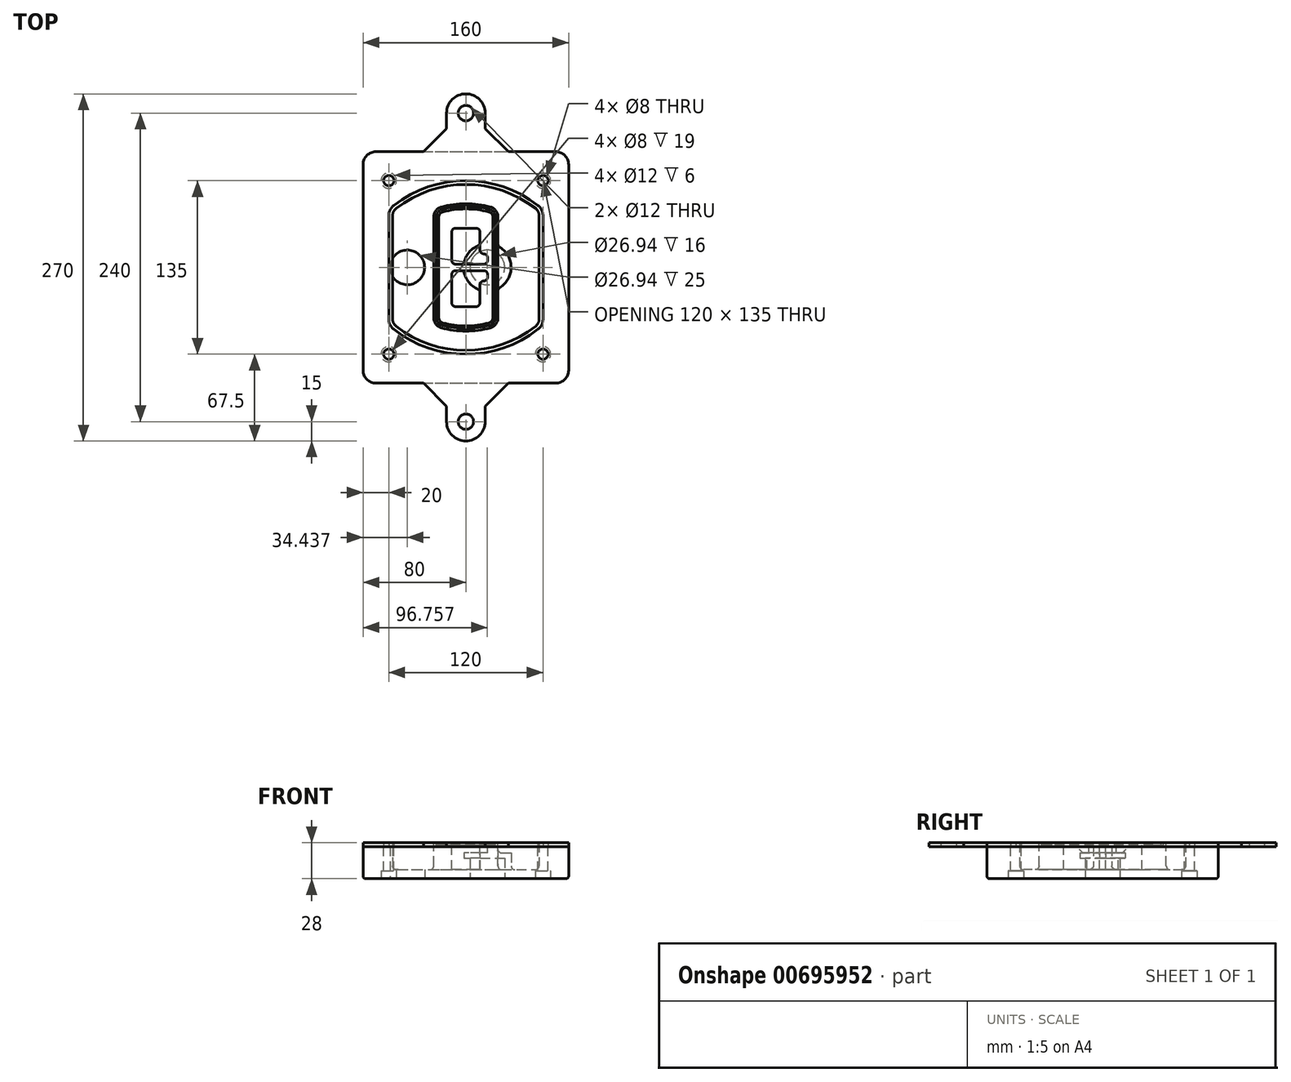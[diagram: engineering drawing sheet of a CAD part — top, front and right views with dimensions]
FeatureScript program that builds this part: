
annotation { "Feature Type Name" : "Feature", "Feature Type Description" : "" }
export const myFeature = defineFeature(function(context is Context, id is Id, definition is map)
    precondition{}
    {
        {
            var Q0;
            Q0=qCreatedBy(makeId("Top.planeOp"),FACE);
            var sketch = newSketch(context, id + "F0", { "sketchPlane" : qUnion([Q0])});
            skPoint(sketch, "E0.rect.middle", {"position": v(0, 0) * mm});
            skLineSegment(sketch, "E1.bottom", {"start": v(-70, -90) * mm, "end": v(70, -90) * mm});
            skLineSegment(sketch, "E1.top", {"start": v(-70, 90) * mm, "end": v(70, 90) * mm});
            skLineSegment(sketch, "E1.left", {"start": v(-80, -80) * mm, "end": v(-80, 80) * mm});
            skLineSegment(sketch, "E1.right", {"start": v(80, -80) * mm, "end": v(80, 80) * mm});
            skLineSegment(sketch, "E2", {"start": v(-80, 90) * mm, "end": v(80, -90) * mm, "construction": true});
            skLineSegment(sketch, "E3", {"start": v(80, 90) * mm, "end": v(-80, -90) * mm, "construction": true});
            skCircle(sketch, "E4", {"center": v(-60, 67.5) * mm, "radius": 4 * mm});
            skCircle(sketch, "E5", {"center": v(60, 67.5) * mm, "radius": 4 * mm});
            skCircle(sketch, "E6", {"center": v(60, -67.5) * mm, "radius": 4 * mm});
            skCircle(sketch, "E7", {"center": v(-60, -67.5) * mm, "radius": 4 * mm});
            skLineSegment(sketch, "E8", {"start": v(-60, 67.5) * mm, "end": v(60, 67.5) * mm, "construction": true});
            skLineSegment(sketch, "E9", {"start": v(60, 67.5) * mm, "end": v(60, -67.5) * mm, "construction": true});
            skLineSegment(sketch, "E10", {"start": v(60, -67.5) * mm, "end": v(-60, -67.5) * mm, "construction": true});
            skLineSegment(sketch, "E11", {"start": v(-60, -67.5) * mm, "end": v(-60, 67.5) * mm, "construction": true});
            skLineSegment(sketch, "E12", {"start": v(-60, 40.3) * mm, "end": v(-60, -40.3) * mm});
            skLineSegment(sketch, "E13", {"start": v(60, 40.3) * mm, "end": v(60, -40.3) * mm});
            skArc(sketch, "E14", {"start": v(56.15, 48.18) * mm, "mid": v(0, 67.5) * mm, "end": v(-56.15, 48.18) * mm});
            skArc(sketch, "E15", {"start": v(-56.15, -48.18) * mm, "mid": v(0, -67.5) * mm, "end": v(56.15, -48.18) * mm});
            skLineSegment(sketch, "E16", {"start": v(-60, 0) * mm, "end": v(60, 0) * mm, "construction": true});
            skPoint(sketch, "E17.visualSharp", {"position": v(-60, -45) * mm});
            skArc(sketch, "E17.filletArc", {"start": v(-60, -40.3) * mm, "mid": v(-58.99, -44.68) * mm, "end": v(-56.15, -48.18) * mm});
            skPoint(sketch, "E18.visualSharp", {"position": v(-60, 45) * mm});
            skArc(sketch, "E18.filletArc", {"start": v(-56.15, 48.18) * mm, "mid": v(-58.99, 44.68) * mm, "end": v(-60, 40.3) * mm});
            skPoint(sketch, "E19.visualSharp", {"position": v(60, 45) * mm});
            skArc(sketch, "E19.filletArc", {"start": v(60, 40.3) * mm, "mid": v(58.99, 44.68) * mm, "end": v(56.15, 48.18) * mm});
            skPoint(sketch, "E20.visualSharp", {"position": v(60, -45) * mm});
            skArc(sketch, "E20.filletArc", {"start": v(56.15, -48.18) * mm, "mid": v(58.99, -44.68) * mm, "end": v(60, -40.3) * mm});
            skPoint(sketch, "E21.visualSharp", {"position": v(-80, 90) * mm});
            skArc(sketch, "E21.filletArc", {"start": v(-70, 90) * mm, "mid": v(-77.07, 87.07) * mm, "end": v(-80, 80) * mm});
            skPoint(sketch, "E22.visualSharp", {"position": v(80, 90) * mm});
            skArc(sketch, "E22.filletArc", {"start": v(80, 80) * mm, "mid": v(77.07, 87.07) * mm, "end": v(70, 90) * mm});
            skPoint(sketch, "E23.visualSharp", {"position": v(80, -90) * mm});
            skArc(sketch, "E23.filletArc", {"start": v(70, -90) * mm, "mid": v(77.07, -87.07) * mm, "end": v(80, -80) * mm});
            skPoint(sketch, "E24.visualSharp", {"position": v(-80, -90) * mm});
            skArc(sketch, "E24.filletArc", {"start": v(-80, -80) * mm, "mid": v(-77.07, -87.07) * mm, "end": v(-70, -90) * mm});
            skArc(sketch, "E25.0", {"start": v(57, 40.3) * mm, "mid": v(56.3, 43.36) * mm, "end": v(54.3, 45.81) * mm});
            skLineSegment(sketch, "E25.1", {"start": v(57, 40.3) * mm, "end": v(57, -40.3) * mm});
            skArc(sketch, "E25.2", {"start": v(54.3, -45.81) * mm, "mid": v(56.3, -43.36) * mm, "end": v(57, -40.3) * mm});
            skArc(sketch, "E25.3", {"start": v(-54.3, -45.81) * mm, "mid": v(0, -64.5) * mm, "end": v(54.3, -45.81) * mm});
            skArc(sketch, "E25.4", {"start": v(-57, -40.3) * mm, "mid": v(-56.3, -43.36) * mm, "end": v(-54.3, -45.81) * mm});
            skArc(sketch, "E25.5", {"start": v(54.3, 45.81) * mm, "mid": v(0, 64.5) * mm, "end": v(-54.3, 45.81) * mm});
            skLineSegment(sketch, "E25.6", {"start": v(-57, 40.3) * mm, "end": v(-57, -40.3) * mm});
            skArc(sketch, "E25.7", {"start": v(-54.3, 45.81) * mm, "mid": v(-56.3, 43.36) * mm, "end": v(-57, 40.3) * mm});
            skArc(sketch, "E26.0", {"start": v(-58.62, 51.33) * mm, "mid": v(-62.58, 46.43) * mm, "end": v(-64, 40.3) * mm});
            skArc(sketch, "E26.1", {"start": v(58.62, 51.33) * mm, "mid": v(0, 71.5) * mm, "end": v(-58.62, 51.33) * mm});
            skArc(sketch, "E26.2", {"start": v(64, 40.3) * mm, "mid": v(62.58, 46.43) * mm, "end": v(58.62, 51.33) * mm});
            skLineSegment(sketch, "E26.3", {"start": v(64, 40.3) * mm, "end": v(64, -40.3) * mm});
            skArc(sketch, "E26.4", {"start": v(58.62, -51.33) * mm, "mid": v(62.58, -46.43) * mm, "end": v(64, -40.3) * mm});
            skLineSegment(sketch, "E26.5", {"start": v(-64, 40.3) * mm, "end": v(-64, -40.3) * mm});
            skArc(sketch, "E26.6", {"start": v(-58.62, -51.33) * mm, "mid": v(0, -71.5) * mm, "end": v(58.62, -51.33) * mm});
            skArc(sketch, "E26.7", {"start": v(-64, -40.3) * mm, "mid": v(-62.58, -46.43) * mm, "end": v(-58.62, -51.33) * mm});
            skSolve(sketch);
        }
        {
            var Q0;
            Q0=makeQuery(id+"F0.imprint","IMPRINT",FACE,{"disambiguationData":[TD([[makeQuery(id+"F0.imprint","IMPRINT",EDGE,{"derivedFrom":sQuery(id+"F0.wireOp",EDGE,"E1.bottom")}),1.0]])]});
            var Q1;
            Q1=makeQuery(id+"F0.imprint","IMPRINT",FACE,{"disambiguationData":[TD([[makeQuery(id+"F0.imprint","IMPRINT",EDGE,{"derivedFrom":sQuery(id+"F0.wireOp",EDGE,"E12")}),1.0]])]});
            var Q2;
            Q2=makeQuery(id+"F0.imprint","IMPRINT",FACE,{"disambiguationData":[TD([[makeQuery(id+"F0.imprint","IMPRINT",EDGE,{"derivedFrom":sQuery(id+"F0.wireOp",EDGE,"E25.0")}),1.0]])]});
            var Q3;
            Q3=makeQuery(id+"F0.imprint","IMPRINT",FACE,{"disambiguationData":[TD([[makeQuery(id+"F0.imprint","IMPRINT",EDGE,{"derivedFrom":sQuery(id+"F0.wireOp",EDGE,"E12")}),-1.0]])]});
            extrude(context, id + "F1", {"entities" : qUnion([Q0, Q1, Q2, Q3]), "oppositeDirection" : true, "depth" : 25 * mm});
        }
        {
            var Q0;
            Q0=makeQuery(id+"F0.imprint","IMPRINT",FACE,{"disambiguationData":[TD([[makeQuery(id+"F0.imprint","IMPRINT",EDGE,{"derivedFrom":sQuery(id+"F0.wireOp",EDGE,"E12")}),1.0]])]});
            extrude(context, id + "F2", {"entities" : qUnion([Q0]), "operationType" : NewBodyOperationType.ADD, "depth" : 3 * mm});
        }
        {
            var Q0;
            Q0=makeQuery(id+"F0.imprint","IMPRINT",FACE,{"disambiguationData":[TD([[makeQuery(id+"F0.imprint","IMPRINT",EDGE,{"derivedFrom":sQuery(id+"F0.wireOp",EDGE,"E25.0")}),1.0]])]});
            extrude(context, id + "F3", {"entities" : qUnion([Q0]), "operationType" : NewBodyOperationType.REMOVE, "oppositeDirection" : true, "depth" : 18 * mm});
        }
        {
            var Q0;
            Q0=makeQuery(id+"F2.opExtrude","CAP_FACE",FACE,{"disambiguationData":[OSD([sQuery(id+"F0.wireOp",EDGE,"E12"),sQuery(id+"F0.wireOp",EDGE,"E13"),sQuery(id+"F0.wireOp",EDGE,"E14"),sQuery(id+"F0.wireOp",EDGE,"E15"),sQuery(id+"F0.wireOp",EDGE,"E17.filletArc"),sQuery(id+"F0.wireOp",EDGE,"E18.filletArc"),sQuery(id+"F0.wireOp",EDGE,"E19.filletArc"),sQuery(id+"F0.wireOp",EDGE,"E20.filletArc"),sQuery(id+"F0.wireOp",EDGE,"E25.0"),sQuery(id+"F0.wireOp",EDGE,"E25.1"),sQuery(id+"F0.wireOp",EDGE,"E25.2"),sQuery(id+"F0.wireOp",EDGE,"E25.3"),sQuery(id+"F0.wireOp",EDGE,"E25.4"),sQuery(id+"F0.wireOp",EDGE,"E25.5"),sQuery(id+"F0.wireOp",EDGE,"E25.6"),sQuery(id+"F0.wireOp",EDGE,"E25.7")])],"isStart":false});
            var sketch = newSketch(context, id + "F4", { "sketchPlane" : qUnion([Q0])});
            skArc(sketch, "E27.0", {"start": v(-19.08, -46.97) * mm, "mid": v(0, -49.5) * mm, "end": v(19.08, -46.97) * mm});
            skArc(sketch, "E28.0", {"start": v(19.08, 46.97) * mm, "mid": v(0, 49.5) * mm, "end": v(-19.08, 46.97) * mm});
            skLineSegment(sketch, "E29", {"start": v(-25, 39.25) * mm, "end": v(-25, -39.25) * mm});
            skLineSegment(sketch, "E30", {"start": v(25, 39.25) * mm, "end": v(25, -39.25) * mm});
            skLineSegment(sketch, "E31", {"start": v(-25, 45.1) * mm, "end": v(25, 45.1) * mm, "construction": true});
            skLineSegment(sketch, "E32", {"start": v(-25, -45.1) * mm, "end": v(25, -45.1) * mm, "construction": true});
            skPoint(sketch, "E33.visualSharp", {"position": v(-25, 45.1) * mm});
            skArc(sketch, "E33.filletArc", {"start": v(-19.08, 46.97) * mm, "mid": v(-23.35, 44.11) * mm, "end": v(-25, 39.25) * mm});
            skPoint(sketch, "E34.visualSharp", {"position": v(25, 45.1) * mm});
            skArc(sketch, "E34.filletArc", {"start": v(25, 39.25) * mm, "mid": v(23.35, 44.11) * mm, "end": v(19.08, 46.97) * mm});
            skPoint(sketch, "E35.visualSharp", {"position": v(25, -45.1) * mm});
            skArc(sketch, "E35.filletArc", {"start": v(19.08, -46.97) * mm, "mid": v(23.35, -44.11) * mm, "end": v(25, -39.25) * mm});
            skPoint(sketch, "E36.visualSharp", {"position": v(-25, -45.1) * mm});
            skArc(sketch, "E36.filletArc", {"start": v(-25, -39.25) * mm, "mid": v(-23.35, -44.11) * mm, "end": v(-19.08, -46.97) * mm});
            skArc(sketch, "E37.0", {"start": v(54.3, 45.81) * mm, "mid": v(0, 64.5) * mm, "end": v(-54.3, 45.81) * mm});
            skArc(sketch, "E37.1", {"start": v(-54.3, 45.81) * mm, "mid": v(-56.3, 43.36) * mm, "end": v(-57, 40.3) * mm});
            skLineSegment(sketch, "E37.2", {"start": v(-57, 40.3) * mm, "end": v(-57, -40.3) * mm});
            skArc(sketch, "E37.3", {"start": v(-57, -40.3) * mm, "mid": v(-56.3, -43.36) * mm, "end": v(-54.3, -45.81) * mm});
            skArc(sketch, "E37.4", {"start": v(-54.3, -45.81) * mm, "mid": v(0, -64.5) * mm, "end": v(54.3, -45.81) * mm});
            skArc(sketch, "E37.5", {"start": v(54.3, -45.81) * mm, "mid": v(56.3, -43.36) * mm, "end": v(57, -40.3) * mm});
            skLineSegment(sketch, "E37.6", {"start": v(57, 40.3) * mm, "end": v(57, -40.3) * mm});
            skArc(sketch, "E37.7", {"start": v(57, 40.3) * mm, "mid": v(56.3, 43.36) * mm, "end": v(54.3, 45.81) * mm});
            skLineSegment(sketch, "E38.0", {"start": v(23, 39.25) * mm, "end": v(23, -39.25) * mm});
            skArc(sketch, "E38.1", {"start": v(18.56, -45.04) * mm, "mid": v(21.76, -42.9) * mm, "end": v(23, -39.25) * mm});
            skArc(sketch, "E38.2", {"start": v(-18.56, -45.04) * mm, "mid": v(0, -47.5) * mm, "end": v(18.56, -45.04) * mm});
            skArc(sketch, "E38.3", {"start": v(-23, -39.25) * mm, "mid": v(-21.76, -42.9) * mm, "end": v(-18.56, -45.04) * mm});
            skLineSegment(sketch, "E38.4", {"start": v(-23, 39.25) * mm, "end": v(-23, -39.25) * mm});
            skArc(sketch, "E38.5", {"start": v(23, 39.25) * mm, "mid": v(21.76, 42.9) * mm, "end": v(18.56, 45.04) * mm});
            skArc(sketch, "E38.6", {"start": v(-18.56, 45.04) * mm, "mid": v(-21.76, 42.9) * mm, "end": v(-23, 39.25) * mm});
            skArc(sketch, "E38.7", {"start": v(18.56, 45.04) * mm, "mid": v(0, 47.5) * mm, "end": v(-18.56, 45.04) * mm});
            skArc(sketch, "E39.0", {"start": v(21, 39.25) * mm, "mid": v(20.18, 41.68) * mm, "end": v(18.04, 43.1) * mm});
            skLineSegment(sketch, "E39.1", {"start": v(21, 39.25) * mm, "end": v(21, -39.25) * mm});
            skArc(sketch, "E39.2", {"start": v(18.04, -43.1) * mm, "mid": v(20.18, -41.68) * mm, "end": v(21, -39.25) * mm});
            skArc(sketch, "E39.3", {"start": v(-18.04, -43.1) * mm, "mid": v(0, -45.5) * mm, "end": v(18.04, -43.1) * mm});
            skArc(sketch, "E39.4", {"start": v(-21, -39.25) * mm, "mid": v(-20.18, -41.68) * mm, "end": v(-18.04, -43.1) * mm});
            skArc(sketch, "E39.5", {"start": v(18.04, 43.1) * mm, "mid": v(0, 45.5) * mm, "end": v(-18.04, 43.1) * mm});
            skLineSegment(sketch, "E39.6", {"start": v(-21, 39.25) * mm, "end": v(-21, -39.25) * mm});
            skArc(sketch, "E39.7", {"start": v(-18.04, 43.1) * mm, "mid": v(-20.18, 41.68) * mm, "end": v(-21, 39.25) * mm});
            skLineSegment(sketch, "E40", {"start": v(-25, 0) * mm, "end": v(25, 0) * mm, "construction": true});
            skLineSegment(sketch, "E41", {"start": v(-11, 5.5) * mm, "end": v(-11, 27.5) * mm});
            skLineSegment(sketch, "E42", {"start": v(-8, 30.5) * mm, "end": v(8, 30.5) * mm});
            skLineSegment(sketch, "E43", {"start": v(11, 27.5) * mm, "end": v(11, 13.5) * mm});
            skLineSegment(sketch, "E44", {"start": v(14, 10.5) * mm, "end": v(14, 10.5) * mm});
            skLineSegment(sketch, "E45", {"start": v(17, 7.5) * mm, "end": v(17, 5.5) * mm});
            skLineSegment(sketch, "E46", {"start": v(14, 2.5) * mm, "end": v(-8, 2.5) * mm});
            skPoint(sketch, "E47.visualSharp", {"position": v(-11, 30.5) * mm});
            skArc(sketch, "E47.filletArc", {"start": v(-8, 30.5) * mm, "mid": v(-10.12, 29.62) * mm, "end": v(-11, 27.5) * mm});
            skPoint(sketch, "E48.visualSharp", {"position": v(11, 30.5) * mm});
            skArc(sketch, "E48.filletArc", {"start": v(11, 27.5) * mm, "mid": v(10.12, 29.62) * mm, "end": v(8, 30.5) * mm});
            skPoint(sketch, "E49.visualSharp", {"position": v(11, 10.5) * mm});
            skArc(sketch, "E49.filletArc", {"start": v(11, 13.5) * mm, "mid": v(11.88, 11.38) * mm, "end": v(14, 10.5) * mm});
            skPoint(sketch, "E50.visualSharp", {"position": v(17, 10.5) * mm});
            skArc(sketch, "E50.filletArc", {"start": v(17, 7.5) * mm, "mid": v(16.12, 9.62) * mm, "end": v(14, 10.5) * mm});
            skPoint(sketch, "E51.visualSharp", {"position": v(17, 2.5) * mm});
            skArc(sketch, "E51.filletArc", {"start": v(14, 2.5) * mm, "mid": v(16.12, 3.38) * mm, "end": v(17, 5.5) * mm});
            skPoint(sketch, "E52.visualSharp", {"position": v(-11, 2.5) * mm});
            skArc(sketch, "E52.filletArc", {"start": v(-11, 5.5) * mm, "mid": v(-10.12, 3.38) * mm, "end": v(-8, 2.5) * mm});
            skLineSegment(sketch, "E53.0.MirrorCS", {"start": v(14, -2.5) * mm, "end": v(-8, -2.5) * mm});
            skArc(sketch, "E54.0.MirrorCS", {"start": v(-11, -5.5) * mm, "mid": v(-10.12, -3.38) * mm, "end": v(-8, -2.5) * mm});
            skLineSegment(sketch, "E55.0.MirrorCS", {"start": v(-11, -5.5) * mm, "end": v(-11, -27.5) * mm});
            skArc(sketch, "E56.0.MirrorCS", {"start": v(-8, -30.5) * mm, "mid": v(-10.12, -29.62) * mm, "end": v(-11, -27.5) * mm});
            skLineSegment(sketch, "E57.0.MirrorCS", {"start": v(-8, -30.5) * mm, "end": v(8, -30.5) * mm});
            skArc(sketch, "E58.0.MirrorCS", {"start": v(11, -27.5) * mm, "mid": v(10.12, -29.62) * mm, "end": v(8, -30.5) * mm});
            skLineSegment(sketch, "E59.0.MirrorCS", {"start": v(11, -27.5) * mm, "end": v(11, -13.5) * mm});
            skArc(sketch, "E60.0.MirrorCS", {"start": v(11, -13.5) * mm, "mid": v(11.88, -11.38) * mm, "end": v(14, -10.5) * mm});
            skArc(sketch, "E61.0.MirrorCS", {"start": v(17, -7.5) * mm, "mid": v(16.12, -9.62) * mm, "end": v(14, -10.5) * mm});
            skLineSegment(sketch, "E62.0.MirrorCS", {"start": v(17, -7.5) * mm, "end": v(17, -5.5) * mm});
            skArc(sketch, "E63.0.MirrorCS", {"start": v(14, -2.5) * mm, "mid": v(16.12, -3.38) * mm, "end": v(17, -5.5) * mm});
            skSolve(sketch);
        }
        {
            var Q0;
            Q0=makeQuery(id+"F4.imprint","IMPRINT",FACE,{"disambiguationData":[TD([[makeQuery(id+"F4.imprint","IMPRINT",EDGE,{"derivedFrom":sQuery(id+"F4.wireOp",EDGE,"E27.0")}),1.0]])]});
            var Q1;
            Q1=makeQuery(id+"F4.imprint","IMPRINT",FACE,{"disambiguationData":[TD([[makeQuery(id+"F4.imprint","IMPRINT",EDGE,{"derivedFrom":sQuery(id+"F4.wireOp",EDGE,"E38.0")}),-1.0]])]});
            var Q2;
            Q2=makeQuery(id+"F4.imprint","IMPRINT",FACE,{"disambiguationData":[TD([[makeQuery(id+"F4.imprint","IMPRINT",EDGE,{"derivedFrom":sQuery(id+"F4.wireOp",EDGE,"E39.0")}),1.0]])]});
            extrude(context, id + "F5", {"entities" : qUnion([Q0, Q1, Q2]), "operationType" : NewBodyOperationType.ADD, "endBound" : BoundingType.UP_TO_NEXT, "oppositeDirection" : true, "depth" : 25 * mm});
        }
        {
            var Q0;
            Q0=makeQuery(id+"F4.imprint","IMPRINT",FACE,{"disambiguationData":[TD([[makeQuery(id+"F4.imprint","IMPRINT",EDGE,{"derivedFrom":sQuery(id+"F4.wireOp",EDGE,"E38.0")}),-1.0]])]});
            extrude(context, id + "F6", {"entities" : qUnion([Q0]), "operationType" : NewBodyOperationType.REMOVE, "oppositeDirection" : true, "depth" : 2 * mm});
        }
        {
            var Q0;
            Q0=makeQuery(id+"F1.opExtrude","CAP_FACE",FACE,{"disambiguationData":[OSD([sQuery(id+"F0.wireOp",EDGE,"E1.bottom"),sQuery(id+"F0.wireOp",EDGE,"E1.top"),sQuery(id+"F0.wireOp",EDGE,"E1.left"),sQuery(id+"F0.wireOp",EDGE,"E1.right"),sQuery(id+"F0.wireOp",EDGE,"E4"),sQuery(id+"F0.wireOp",EDGE,"E5"),sQuery(id+"F0.wireOp",EDGE,"E6"),sQuery(id+"F0.wireOp",EDGE,"E7"),sQuery(id+"F0.wireOp",EDGE,"E21.filletArc"),sQuery(id+"F0.wireOp",EDGE,"E22.filletArc"),sQuery(id+"F0.wireOp",EDGE,"E23.filletArc"),sQuery(id+"F0.wireOp",EDGE,"E24.filletArc")])],"isStart":false});
            var sketch = newSketch(context, id + "F7", { "sketchPlane" : qUnion([Q0])});
            skCircle(sketch, "E64", {"center": v(16.76, 0) * mm, "radius": 13.47 * mm});
            skCircle(sketch, "E65", {"center": v(-45.56, 0) * mm, "radius": 13.47 * mm});
            skLineSegment(sketch, "E66", {"start": v(80, 0) * mm, "end": v(-80, 0) * mm});
            skCircle(sketch, "E67", {"center": v(16.76, 0) * mm, "radius": 18.47 * mm});
            skCircle(sketch, "E68", {"center": v(60, -67.5) * mm, "radius": 6 * mm});
            skCircle(sketch, "E69", {"center": v(-60, -67.5) * mm, "radius": 6 * mm});
            skCircle(sketch, "E70", {"center": v(-60, 67.5) * mm, "radius": 6 * mm});
            skCircle(sketch, "E71", {"center": v(60, 67.5) * mm, "radius": 6 * mm});
            skSolve(sketch);
        }
        {
            var Q0;
            {var subQ1=sQuery(id+"F7.wireOp",EDGE,"E66");var subQ4=sQuery(id+"F7.wireOp",EDGE,"E64");var subQ6=makeQuery(id+"F7.imprint","INTERSECT",VERTEX,{"disambiguationData":[OD(0.0)],"derivedFrom":[subQ4,subQ1]});Q0=makeQuery(id+"F7.imprint","IMPRINT",FACE,{"disambiguationData":[TD([[makeQuery(id+"F7.imprint","IMPRINT",EDGE,{"disambiguationData":[TD([[subQ6,-1.0]])],"derivedFrom":subQ4}),-1.0]])]});}
            var Q1;
            {var subQ0=sQuery(id+"F7.wireOp",EDGE,"E66");var subQ1=sQuery(id+"F7.wireOp",EDGE,"E64");var subQ3=makeQuery(id+"F7.imprint","INTERSECT",VERTEX,{"disambiguationData":[OD(0.0)],"derivedFrom":[subQ1,subQ0]});Q1=makeQuery(id+"F7.imprint","IMPRINT",FACE,{"disambiguationData":[TD([[makeQuery(id+"F7.imprint","IMPRINT",EDGE,{"disambiguationData":[TD([[subQ3,-1.0]])],"derivedFrom":subQ1}),1.0]])]});}
            var Q2;
            {var subQ0=sQuery(id+"F7.wireOp",EDGE,"E66");var subQ1=sQuery(id+"F7.wireOp",EDGE,"E64");var subQ3=makeQuery(id+"F7.imprint","INTERSECT",VERTEX,{"disambiguationData":[OD(0.0)],"derivedFrom":[subQ1,subQ0]});Q2=makeQuery(id+"F7.imprint","IMPRINT",FACE,{"disambiguationData":[TD([[makeQuery(id+"F7.imprint","IMPRINT",EDGE,{"disambiguationData":[TD([[subQ3,1.0]])],"derivedFrom":subQ1}),1.0]])]});}
            var Q3;
            {var subQ1=sQuery(id+"F7.wireOp",EDGE,"E66");var subQ4=sQuery(id+"F7.wireOp",EDGE,"E64");var subQ6=makeQuery(id+"F7.imprint","INTERSECT",VERTEX,{"disambiguationData":[OD(0.0)],"derivedFrom":[subQ4,subQ1]});Q3=makeQuery(id+"F7.imprint","IMPRINT",FACE,{"disambiguationData":[TD([[makeQuery(id+"F7.imprint","IMPRINT",EDGE,{"disambiguationData":[TD([[subQ6,1.0]])],"derivedFrom":subQ4}),-1.0]])]});}
            extrude(context, id + "F8", {"entities" : qUnion([Q0, Q1, Q2, Q3]), "operationType" : NewBodyOperationType.ADD, "oppositeDirection" : true, "depth" : 20 * mm});
        }
        {
            var Q0;
            {var subQ0=sQuery(id+"F7.wireOp",EDGE,"E66");var subQ1=sQuery(id+"F7.wireOp",EDGE,"E64");var subQ3=makeQuery(id+"F7.imprint","INTERSECT",VERTEX,{"disambiguationData":[OD(0.0)],"derivedFrom":[subQ1,subQ0]});Q0=makeQuery(id+"F7.imprint","IMPRINT",FACE,{"disambiguationData":[TD([[makeQuery(id+"F7.imprint","IMPRINT",EDGE,{"disambiguationData":[TD([[subQ3,-1.0]])],"derivedFrom":subQ1}),1.0]])]});}
            var Q1;
            {var subQ0=sQuery(id+"F7.wireOp",EDGE,"E66");var subQ1=sQuery(id+"F7.wireOp",EDGE,"E64");var subQ3=makeQuery(id+"F7.imprint","INTERSECT",VERTEX,{"disambiguationData":[OD(0.0)],"derivedFrom":[subQ1,subQ0]});Q1=makeQuery(id+"F7.imprint","IMPRINT",FACE,{"disambiguationData":[TD([[makeQuery(id+"F7.imprint","IMPRINT",EDGE,{"disambiguationData":[TD([[subQ3,1.0]])],"derivedFrom":subQ1}),1.0]])]});}
            extrude(context, id + "F9", {"entities" : qUnion([Q0, Q1]), "operationType" : NewBodyOperationType.REMOVE, "oppositeDirection" : true, "depth" : 16 * mm});
        }
        {
            var Q0;
            {var subQ0=sQuery(id+"F7.wireOp",EDGE,"E66");var subQ1=sQuery(id+"F7.wireOp",EDGE,"E65");var subQ3=makeQuery(id+"F7.imprint","INTERSECT",VERTEX,{"disambiguationData":[OD(0.0)],"derivedFrom":[subQ1,subQ0]});Q0=makeQuery(id+"F7.imprint","IMPRINT",FACE,{"disambiguationData":[TD([[makeQuery(id+"F7.imprint","IMPRINT",EDGE,{"disambiguationData":[TD([[subQ3,-1.0]])],"derivedFrom":subQ1}),1.0]])]});}
            var Q1;
            {var subQ0=sQuery(id+"F7.wireOp",EDGE,"E66");var subQ1=sQuery(id+"F7.wireOp",EDGE,"E65");var subQ3=makeQuery(id+"F7.imprint","INTERSECT",VERTEX,{"disambiguationData":[OD(0.0)],"derivedFrom":[subQ1,subQ0]});Q1=makeQuery(id+"F7.imprint","IMPRINT",FACE,{"disambiguationData":[TD([[makeQuery(id+"F7.imprint","IMPRINT",EDGE,{"disambiguationData":[TD([[subQ3,1.0]])],"derivedFrom":subQ1}),1.0]])]});}
            extrude(context, id + "F10", {"entities" : qUnion([Q0, Q1]), "operationType" : NewBodyOperationType.REMOVE, "oppositeDirection" : true, "depth" : 25 * mm});
        }
        {
            var Q0;
            Q0=makeQuery(id+"F7.imprint","IMPRINT",FACE,{"disambiguationData":[TD([[makeQuery(id+"F7.imprint","IMPRINT",EDGE,{"derivedFrom":sQuery(id+"F7.wireOp",EDGE,"E68")}),1.0]])]});
            var Q1;
            Q1=makeQuery(id+"F7.imprint","IMPRINT",FACE,{"disambiguationData":[TD([[makeQuery(id+"F7.imprint","IMPRINT",EDGE,{"derivedFrom":makeQuery(id+"F1.opExtrude","CAP_EDGE",EDGE,{"disambiguationData":[OSD([sQuery(id+"F0.wireOp",EDGE,"E5")])],"isStart":false})}),-1.0]])]});
            var Q2;
            Q2=makeQuery(id+"F7.imprint","IMPRINT",FACE,{"disambiguationData":[TD([[makeQuery(id+"F7.imprint","IMPRINT",EDGE,{"derivedFrom":sQuery(id+"F7.wireOp",EDGE,"E69")}),1.0]])]});
            var Q3;
            Q3=makeQuery(id+"F7.imprint","IMPRINT",FACE,{"disambiguationData":[TD([[makeQuery(id+"F7.imprint","IMPRINT",EDGE,{"derivedFrom":makeQuery(id+"F1.opExtrude","CAP_EDGE",EDGE,{"disambiguationData":[OSD([sQuery(id+"F0.wireOp",EDGE,"E4")])],"isStart":false})}),-1.0]])]});
            var Q4;
            Q4=makeQuery(id+"F7.imprint","IMPRINT",FACE,{"disambiguationData":[TD([[makeQuery(id+"F7.imprint","IMPRINT",EDGE,{"derivedFrom":sQuery(id+"F7.wireOp",EDGE,"E70")}),1.0]])]});
            var Q5;
            Q5=makeQuery(id+"F7.imprint","IMPRINT",FACE,{"disambiguationData":[TD([[makeQuery(id+"F7.imprint","IMPRINT",EDGE,{"derivedFrom":makeQuery(id+"F1.opExtrude","CAP_EDGE",EDGE,{"disambiguationData":[OSD([sQuery(id+"F0.wireOp",EDGE,"E7")])],"isStart":false})}),-1.0]])]});
            var Q6;
            Q6=makeQuery(id+"F7.imprint","IMPRINT",FACE,{"disambiguationData":[TD([[makeQuery(id+"F7.imprint","IMPRINT",EDGE,{"derivedFrom":sQuery(id+"F7.wireOp",EDGE,"E71")}),1.0]])]});
            var Q7;
            Q7=makeQuery(id+"F7.imprint","IMPRINT",FACE,{"disambiguationData":[TD([[makeQuery(id+"F7.imprint","IMPRINT",EDGE,{"derivedFrom":makeQuery(id+"F1.opExtrude","CAP_EDGE",EDGE,{"disambiguationData":[OSD([sQuery(id+"F0.wireOp",EDGE,"E6")])],"isStart":false})}),-1.0]])]});
            extrude(context, id + "F11", {"entities" : qUnion([Q0, Q1, Q2, Q3, Q4, Q5, Q6, Q7]), "operationType" : NewBodyOperationType.REMOVE, "oppositeDirection" : true, "depth" : 6 * mm});
        }
        {
            var Q0;
            Q0=makeQuery(id+"F9.boolean.opBoolean","COPY",FACE,{"derivedFrom":makeQuery(id+"F9.opExtrude","CAP_FACE",FACE,{"disambiguationData":[OSD([sQuery(id+"F7.wireOp",EDGE,"E64")])],"isStart":false})});
            var sketch = newSketch(context, id + "F12", { "sketchPlane" : qUnion([Q0])});
            skArc(sketch, "E72.0", {"start": v(11, 17.55) * mm, "mid": v(2.57, 11.82) * mm, "end": v(-1.54, 2.5) * mm});
            skArc(sketch, "E72.1", {"start": v(-1.54, -2.5) * mm, "mid": v(2.57, -11.82) * mm, "end": v(11, -17.55) * mm});
            skLineSegment(sketch, "E73", {"start": v(-1.54, -2.5) * mm, "end": v(14, -2.5) * mm});
            skLineSegment(sketch, "E74.0", {"start": v(14, 2.5) * mm, "end": v(-1.54, 2.5) * mm});
            skArc(sketch, "E74.1", {"start": v(14, 2.5) * mm, "mid": v(16.12, 3.38) * mm, "end": v(17, 5.5) * mm});
            skLineSegment(sketch, "E74.2", {"start": v(17, 7.5) * mm, "end": v(17, 5.5) * mm});
            skArc(sketch, "E74.3", {"start": v(17, 7.5) * mm, "mid": v(16.12, 9.62) * mm, "end": v(14, 10.5) * mm});
            skArc(sketch, "E74.4", {"start": v(11, 13.5) * mm, "mid": v(11.88, 11.38) * mm, "end": v(14, 10.5) * mm});
            skLineSegment(sketch, "E74.5", {"start": v(11, 17.55) * mm, "end": v(11, 13.5) * mm});
            skLineSegment(sketch, "E74.7", {"start": v(14, -2.5) * mm, "end": v(-1.54, -2.5) * mm});
            skArc(sketch, "E74.8", {"start": v(14, -2.5) * mm, "mid": v(16.12, -3.38) * mm, "end": v(17, -5.5) * mm});
            skLineSegment(sketch, "E74.9", {"start": v(17, -7.5) * mm, "end": v(17, -5.5) * mm});
            skArc(sketch, "E74.10", {"start": v(17, -7.5) * mm, "mid": v(16.12, -9.62) * mm, "end": v(14, -10.5) * mm});
            skArc(sketch, "E74.11", {"start": v(11, -13.5) * mm, "mid": v(11.88, -11.38) * mm, "end": v(14, -10.5) * mm});
            skLineSegment(sketch, "E74.12", {"start": v(11, -17.55) * mm, "end": v(11, -13.5) * mm});
            skPoint(sketch, "E75.orphan", {"position": v(11, -27.5) * mm});
            skPoint(sketch, "E76.orphan", {"position": v(-8, -2.5) * mm});
            skPoint(sketch, "E77.orphan", {"position": v(-8, 2.5) * mm});
            skPoint(sketch, "E78.orphan", {"position": v(11, 27.5) * mm});
            skSolve(sketch);
        }
        {
            var Q0;
            {var subQ7=sQuery(id+"F12.wireOp",EDGE,"E72.0");var subQ14=sQuery(id+"F12.wireOp",EDGE,"E72.1");var subQ16=sQuery(id+"F12.wireOp",EDGE,"E74.1");var subQ18=sQuery(id+"F12.wireOp",EDGE,"E74.8");Q0=qUnion([makeQuery(id+"F12.imprint","IMPRINT",FACE,{"disambiguationData":[TD([[makeQuery(id+"F12.imprint","IMPRINT",EDGE,{"derivedFrom":subQ7}),1.0]])]}),makeQuery(id+"F12.imprint","IMPRINT",FACE,{"disambiguationData":[TD([[makeQuery(id+"F12.imprint","IMPRINT",EDGE,{"derivedFrom":subQ14}),1.0]])]}),makeQuery(id+"F12.imprint","IMPRINT",FACE,{"disambiguationData":[TD([[makeQuery(id+"F12.imprint","IMPRINT",EDGE,{"derivedFrom":subQ16}),1.0]])]}),makeQuery(id+"F12.imprint","IMPRINT",FACE,{"disambiguationData":[TD([[makeQuery(id+"F12.imprint","IMPRINT",EDGE,{"derivedFrom":subQ18}),-1.0]])]})]);}
            var Q1;
            Q1=makeQuery(id+"F5.boolean.opBoolean","SPLIT",FACE,{"disambiguationData":[TD([makeQuery(id+"F5.opExtrude","SWEPT_FACE",FACE,{"disambiguationData":[OSD([sQuery(id+"F4.wireOp",EDGE,"E41")])]})])],"derivedFrom":makeQuery(id+"F3.boolean.opBoolean","COPY",FACE,{"derivedFrom":makeQuery(id+"F3.opExtrude","CAP_FACE",FACE,{"disambiguationData":[OSD([sQuery(id+"F0.wireOp",EDGE,"E25.0"),sQuery(id+"F0.wireOp",EDGE,"E25.1"),sQuery(id+"F0.wireOp",EDGE,"E25.2"),sQuery(id+"F0.wireOp",EDGE,"E25.3"),sQuery(id+"F0.wireOp",EDGE,"E25.4"),sQuery(id+"F0.wireOp",EDGE,"E25.5"),sQuery(id+"F0.wireOp",EDGE,"E25.6"),sQuery(id+"F0.wireOp",EDGE,"E25.7")])],"isStart":false})})});
            extrude(context, id + "F13", {"entities" : qUnion([Q0]), "operationType" : NewBodyOperationType.REMOVE, "endBound" : BoundingType.UP_TO_SURFACE, "endBoundEntityFace" : qUnion([Q1]), "depth" : 25 * mm});
        }
        {
            var Q0;
            Q0=makeQuery(id+"F3.boolean.opBoolean","COPY",EDGE,{"derivedFrom":makeQuery(id+"F3.opExtrude","CAP_EDGE",EDGE,{"disambiguationData":[OSD([sQuery(id+"F0.wireOp",EDGE,"E25.6")])],"isStart":false})});
            var Q1;
            Q1=makeQuery(id+"F8.boolean.opBoolean","INTERSECT",EDGE,{"derivedFrom":[makeQuery(id+"F5.opExtrude","SWEPT_FACE",FACE,{"disambiguationData":[OSD([sQuery(id+"F4.wireOp",EDGE,"E30")])]}),makeQuery(id+"F8.opExtrude","CAP_FACE",FACE,{"disambiguationData":[OSD([sQuery(id+"F7.wireOp",EDGE,"E67")])],"isStart":false})]});
            var Q2;
            Q2=makeQuery(id+"F8.boolean.opBoolean","INTERSECT",EDGE,{"disambiguationData":[OD(1.0)],"derivedFrom":[makeQuery(id+"F5.opExtrude","SWEPT_FACE",FACE,{"disambiguationData":[OSD([sQuery(id+"F4.wireOp",EDGE,"E30")])]}),makeQuery(id+"F8.opExtrude","SWEPT_FACE",FACE,{"disambiguationData":[OSD([sQuery(id+"F7.wireOp",EDGE,"E67")])]})]});
            var Q3;
            {var subQ0=sQuery(id+"F4.wireOp",EDGE,"E30");Q3=makeQuery(id+"F8.boolean.opBoolean","SPLIT",EDGE,{"disambiguationData":[TD([makeQuery(id+"F5.opExtrude","SWEPT_FACE",FACE,{"disambiguationData":[OSD([sQuery(id+"F4.wireOp",EDGE,"E35.filletArc")])]})])],"derivedFrom":makeQuery(id+"F5.opExtrude","CAP_EDGE",EDGE,{"disambiguationData":[OSD([subQ0])],"isStart":false})});}
            var Q4;
            {var subQ0=sQuery(id+"F0.wireOp",EDGE,"E25.7");var subQ1=sQuery(id+"F0.wireOp",EDGE,"E25.1");var subQ2=sQuery(id+"F0.wireOp",EDGE,"E25.6");var subQ3=sQuery(id+"F0.wireOp",EDGE,"E25.5");var subQ4=sQuery(id+"F0.wireOp",EDGE,"E25.4");var subQ5=sQuery(id+"F0.wireOp",EDGE,"E25.0");var subQ6=sQuery(id+"F0.wireOp",EDGE,"E25.2");var subQ7=sQuery(id+"F0.wireOp",EDGE,"E25.3");Q4=makeQuery(id+"F8.boolean.opBoolean","INTERSECT",EDGE,{"derivedFrom":[makeQuery(id+"F5.boolean.opBoolean","SPLIT",FACE,{"disambiguationData":[TD([makeQuery(id+"F2.opExtrude","SWEPT_FACE",FACE,{"disambiguationData":[OSD([subQ5])]})])],"derivedFrom":makeQuery(id+"F3.boolean.opBoolean","COPY",FACE,{"derivedFrom":makeQuery(id+"F3.opExtrude","CAP_FACE",FACE,{"disambiguationData":[OSD([subQ5,subQ1,subQ6,subQ7,subQ4,subQ3,subQ2,subQ0])],"isStart":false})})}),makeQuery(id+"F8.opExtrude","SWEPT_FACE",FACE,{"disambiguationData":[OSD([sQuery(id+"F7.wireOp",EDGE,"E67")])]})]});}
            var Q5;
            Q5=makeQuery(id+"F8.boolean.opBoolean","INTERSECT",EDGE,{"disambiguationData":[OD(0.0)],"derivedFrom":[makeQuery(id+"F5.opExtrude","SWEPT_FACE",FACE,{"disambiguationData":[OSD([sQuery(id+"F4.wireOp",EDGE,"E30")])]}),makeQuery(id+"F8.opExtrude","SWEPT_FACE",FACE,{"disambiguationData":[OSD([sQuery(id+"F7.wireOp",EDGE,"E67")])]})]});
            fillet(context, id + "F14", {"entities" : qUnion([Q0, Q1, Q2, Q3, Q4, Q5]), "radius" : 3 * mm, "tangentPropagation" : true, "allowEdgeOverflow" : false});
        }
        {
            var Q0;
            Q0=makeQuery(id+"F1.opExtrude","CAP_EDGE",EDGE,{"disambiguationData":[OSD([sQuery(id+"F0.wireOp",EDGE,"E1.bottom")])],"isStart":false});
            fillet(context, id + "F15", {"entities" : qUnion([Q0]), "radius" : 2 * mm, "tangentPropagation" : true, "allowEdgeOverflow" : false});
        }
        {
            var Q0;
            {var subQ0=sQuery(id+"F0.wireOp",EDGE,"E21.filletArc");var subQ1=sQuery(id+"F0.wireOp",EDGE,"E7");var subQ2=sQuery(id+"F0.wireOp",EDGE,"E6");var subQ3=sQuery(id+"F0.wireOp",EDGE,"E5");var subQ4=sQuery(id+"F0.wireOp",EDGE,"E4");var subQ5=sQuery(id+"F0.wireOp",EDGE,"E22.filletArc");var subQ6=sQuery(id+"F0.wireOp",EDGE,"E1.bottom");var subQ7=sQuery(id+"F0.wireOp",EDGE,"E1.right");var subQ8=sQuery(id+"F0.wireOp",EDGE,"E1.top");var subQ9=sQuery(id+"F0.wireOp",EDGE,"E1.left");var subQ10=sQuery(id+"F0.wireOp",EDGE,"E23.filletArc");var subQ11=sQuery(id+"F0.wireOp",EDGE,"E24.filletArc");Q0=makeQuery(id+"F2.boolean.opBoolean","SPLIT",FACE,{"disambiguationData":[TD([makeQuery(id+"F1.opExtrude","SWEPT_FACE",FACE,{"disambiguationData":[OSD([subQ6])]})])],"derivedFrom":makeQuery(id+"F1.opExtrude","CAP_FACE",FACE,{"disambiguationData":[OSD([subQ6,subQ8,subQ9,subQ7,subQ4,subQ3,subQ2,subQ1,subQ0,subQ5,subQ10,subQ11])],"isStart":true})});}
            var sketch = newSketch(context, id + "F16", { "sketchPlane" : qUnion([Q0])});
            skLineSegment(sketch, "E79.0", {"start": v(-70, 90) * mm, "end": v(70, 90) * mm});
            skArc(sketch, "E79.1", {"start": v(-70, 90) * mm, "mid": v(-77.07, 87.07) * mm, "end": v(-80, 80) * mm});
            skLineSegment(sketch, "E79.2", {"start": v(-80, -80) * mm, "end": v(-80, 80) * mm});
            skArc(sketch, "E79.3", {"start": v(80, 80) * mm, "mid": v(77.07, 87.07) * mm, "end": v(70, 90) * mm});
            skLineSegment(sketch, "E79.4", {"start": v(80, -80) * mm, "end": v(80, 80) * mm});
            skArc(sketch, "E79.5", {"start": v(70, -90) * mm, "mid": v(77.07, -87.07) * mm, "end": v(80, -80) * mm});
            skLineSegment(sketch, "E79.6", {"start": v(-70, -90) * mm, "end": v(70, -90) * mm});
            skArc(sketch, "E79.7", {"start": v(-80, -80) * mm, "mid": v(-77.07, -87.07) * mm, "end": v(-70, -90) * mm});
            skCircle(sketch, "E79.8", {"center": v(-60, 67.5) * mm, "radius": 4 * mm});
            skCircle(sketch, "E79.9", {"center": v(60, 67.5) * mm, "radius": 4 * mm});
            skCircle(sketch, "E79.10", {"center": v(60, -67.5) * mm, "radius": 4 * mm});
            skCircle(sketch, "E79.11", {"center": v(-60, -67.5) * mm, "radius": 4 * mm});
            skArc(sketch, "E79.12", {"start": v(-56.15, -48.18) * mm, "mid": v(0, -67.5) * mm, "end": v(56.15, -48.18) * mm});
            skArc(sketch, "E79.13", {"start": v(-60, -40.3) * mm, "mid": v(-58.99, -44.68) * mm, "end": v(-56.15, -48.18) * mm});
            skLineSegment(sketch, "E79.14", {"start": v(-60, 40.3) * mm, "end": v(-60, -40.3) * mm});
            skArc(sketch, "E79.15", {"start": v(-56.15, 48.18) * mm, "mid": v(-58.99, 44.68) * mm, "end": v(-60, 40.3) * mm});
            skArc(sketch, "E79.16", {"start": v(56.15, 48.18) * mm, "mid": v(0, 67.5) * mm, "end": v(-56.15, 48.18) * mm});
            skArc(sketch, "E79.17", {"start": v(60, 40.3) * mm, "mid": v(58.99, 44.68) * mm, "end": v(56.15, 48.18) * mm});
            skLineSegment(sketch, "E79.18", {"start": v(60, 40.3) * mm, "end": v(60, -40.3) * mm});
            skArc(sketch, "E79.19", {"start": v(56.15, -48.18) * mm, "mid": v(58.99, -44.68) * mm, "end": v(60, -40.3) * mm});
            skLineSegment(sketch, "E80", {"start": v(0, 90) * mm, "end": v(0, 120) * mm, "construction": true});
            skCircle(sketch, "E81", {"center": v(0, 120) * mm, "radius": 6 * mm});
            skArc(sketch, "E82", {"start": v(15, 120) * mm, "mid": v(0, 135) * mm, "end": v(-15, 120) * mm});
            skLineSegment(sketch, "E83", {"start": v(-15, 120) * mm, "end": v(-15, 108) * mm});
            skLineSegment(sketch, "E84", {"start": v(-15, 108) * mm, "end": v(-33, 90) * mm});
            skLineSegment(sketch, "E85", {"start": v(15, 120) * mm, "end": v(15, 108) * mm});
            skLineSegment(sketch, "E86", {"start": v(15, 108) * mm, "end": v(33, 90) * mm});
            skLineSegment(sketch, "E87", {"start": v(-80, 0) * mm, "end": v(80, 0) * mm, "construction": true});
            skLineSegment(sketch, "E88.MirrorCS", {"start": v(-15, -120) * mm, "end": v(-15, -108) * mm});
            skArc(sketch, "E89.MirrorCS", {"start": v(15, -120) * mm, "mid": v(0, -135) * mm, "end": v(-15, -120) * mm});
            skCircle(sketch, "E90.MirrorC", {"center": v(0, -120) * mm, "radius": 6 * mm});
            skLineSegment(sketch, "E91.MirrorCS", {"start": v(15, -120) * mm, "end": v(15, -108) * mm});
            skLineSegment(sketch, "E92.MirrorCS", {"start": v(15, -108) * mm, "end": v(33, -90) * mm});
            skLineSegment(sketch, "E93.MirrorCS", {"start": v(0, -90) * mm, "end": v(0, -120) * mm, "construction": true});
            skLineSegment(sketch, "E94.MirrorCS", {"start": v(-15, -108) * mm, "end": v(-33, -90) * mm});
            skSolve(sketch);
        }
        {
            var Q0;
            Q0 = qSketchRegion(id + "F16", true);
            var Q1;
            Q1=makeQuery(id+"F2.opExtrude","CAP_FACE",FACE,{"disambiguationData":[OSD([sQuery(id+"F0.wireOp",EDGE,"E12"),sQuery(id+"F0.wireOp",EDGE,"E13"),sQuery(id+"F0.wireOp",EDGE,"E14"),sQuery(id+"F0.wireOp",EDGE,"E15"),sQuery(id+"F0.wireOp",EDGE,"E17.filletArc"),sQuery(id+"F0.wireOp",EDGE,"E18.filletArc"),sQuery(id+"F0.wireOp",EDGE,"E19.filletArc"),sQuery(id+"F0.wireOp",EDGE,"E20.filletArc"),sQuery(id+"F0.wireOp",EDGE,"E25.0"),sQuery(id+"F0.wireOp",EDGE,"E25.1"),sQuery(id+"F0.wireOp",EDGE,"E25.2"),sQuery(id+"F0.wireOp",EDGE,"E25.3"),sQuery(id+"F0.wireOp",EDGE,"E25.4"),sQuery(id+"F0.wireOp",EDGE,"E25.5"),sQuery(id+"F0.wireOp",EDGE,"E25.6"),sQuery(id+"F0.wireOp",EDGE,"E25.7")])],"isStart":false});
            extrude(context, id + "F17", {"entities" : qUnion([Q0]), "endBound" : BoundingType.UP_TO_SURFACE, "depth" : 25 * mm, "endBoundEntityFace" : qUnion([Q1]), "offsetDistance" : 25 * mm});
        }
    });
